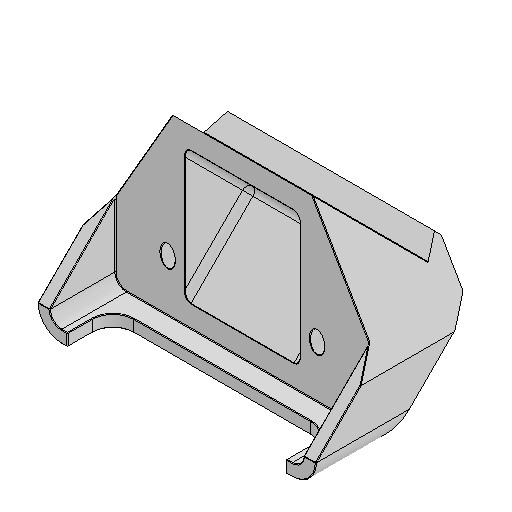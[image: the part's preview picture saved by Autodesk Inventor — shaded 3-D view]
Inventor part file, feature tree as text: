
AUTODESK INVENTOR PART (.ipt)
format: ipt  version: 2024.3 (Build 283343000, 343)  size: 491,520 bytes
history: native  units: mm
features: other x20, extrude x12, sketch x9, fillet x7, plane x5, mirror x2
ambient origin geometry x8: Origin, YZ Plane, XZ Plane, XY Plane, X Axis, Y Axis, Z Axis, Center Point
bodies: Body1 (feature_tree)
feature tree (55):
  other  "實體1"
  sketch  "草圖1"
  plane  "工作平面2"
  extrude  "擠出1"  Depth=0.25mm
  plane  "工作平面1"
  extrude  "擠出2"  Depth=5.0mm
  extrude  "擠出3"  Depth=30.0mm TaperAngle=0.0deg
  extrude  "擠出4"  Depth=30.0mm TaperAngle=0.0deg
  extrude  "擠出5"  Depth=0.125mm
  other  "直接編輯1"
  fillet  "圓角1"  Radius=0.25mm
  sketch  "草圖5"
  extrude  "擠出6"  Depth=2.5mm
  plane  "工作平面3"
  extrude  "擠出7"  Depth=3.085047mm
  fillet  "圓角2"  Radius=13.5mm
  plane  "工作平面4"
  mirror  "鏡射1"
  sketch  "草圖6"
  extrude  "擠出8"  Depth=10.0mm TaperAngle=0.0deg
  fillet  "圓角3"  Radius=10.0mm
  fillet  "圓角4"  Radius=0.25mm
  plane  "工作平面5"
  sketch  "草圖8"
  extrude  "擠出9"  TaperAngle=0.0deg  [1 undecoded]
  extrude  "擠出10"  TaperAngle=0.0deg  [1 undecoded]
  extrude  "擠出11"  TaperAngle=0.0deg  [1 undecoded]
  fillet  "圓角5"  Radius=25.0mm
  fillet  "圓角6"  Radius=0.25mm
  fillet  "圓角7"  Radius=3.0mm
  extrude  "擠出12"  Depth=5.9mm
  mirror  "鏡射2"
  other  "參考1"
  sketch  "草圖2"
  other  "參考2"
  other  "參考3"
  other  "參考4"
  other  "參考5"
  other  "參考6"
  other  "參考7"
  sketch  "草圖3"
  other  "參考10"
  other  "參考11"
  sketch  "草圖4"
  other  "參考12"
  other  "參考13"
  sketch  "草圖7"
  other  "參考14"
  sketch  "草圖9"
  other  "Atom_3_Lite_Upgrade.iam"
  other  "eBox:1"
  other  "Atom_3_lite:1"
  other  "移動1"
  other  "移動2"
  other  "移動3"
note: 3 required parameter values undecoded (feature->parameter linkage not recoverable at this tier; creation-order binding heuristic only, values carry confidence <= 0.55)
